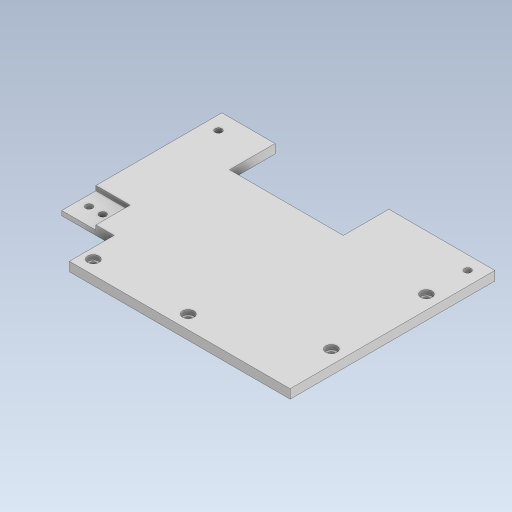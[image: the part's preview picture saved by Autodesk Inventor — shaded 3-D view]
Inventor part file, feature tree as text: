
AUTODESK INVENTOR PART (.ipt)
format: ipt  version: 2023.5 (Build 275446000, 446)  size: 334,336 bytes
history: native  units: in
note: dims shown in document units (in); Inventor stores cm internally (conversion verified against a paired STEP export)
features: extrude x2, sketch x1
ambient origin geometry x8: Origin, YZ Plane, XZ Plane, XY Plane, X Axis, Y Axis, Z Axis, Center Point
bodies: Solid1 (feature_tree)
feature tree (3):
  sketch  "Sketch1"  dims[d28=0.1575in d29=0.0in d30=0.0787in d31=0.0in d32=0.4724in d33=0.2953in d34=0.2953in d35=0.4724in d36=0.0in d37=0.0in d39=0.315in]
  extrude  "Extrusion1"  Depth=0.0787in TaperAngle=0.0deg
  extrude  "Extrusion2"  Depth=0.315in
